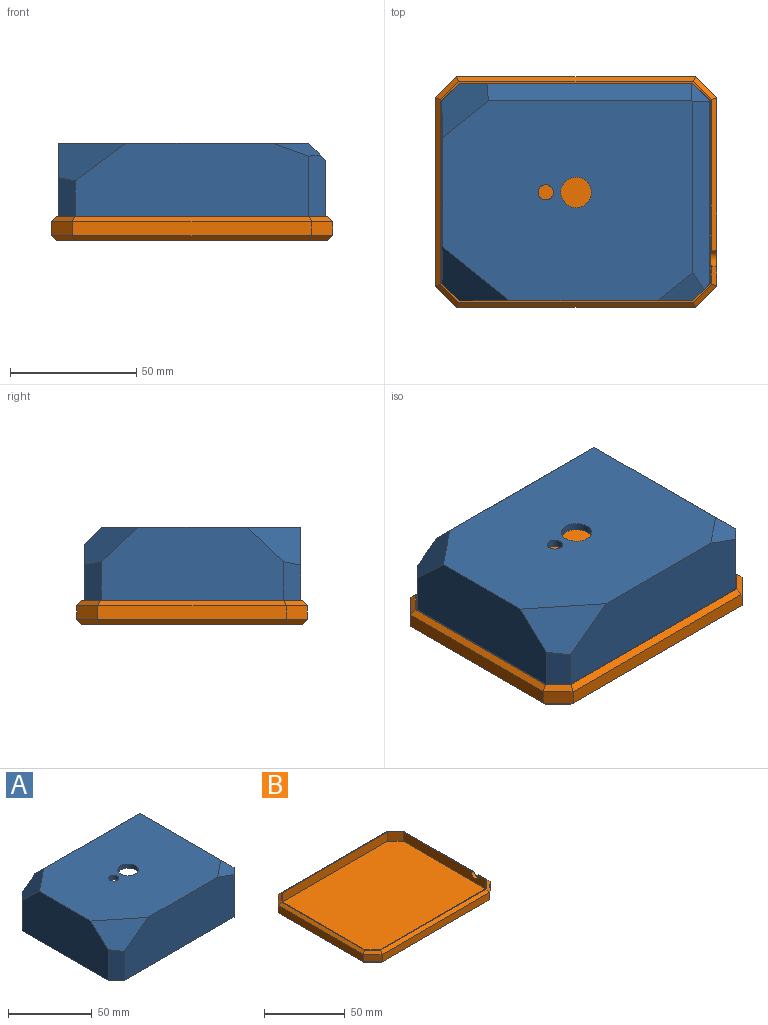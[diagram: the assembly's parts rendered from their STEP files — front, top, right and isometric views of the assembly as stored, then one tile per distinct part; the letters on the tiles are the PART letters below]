
ASSEMBLY  parts=2 mates=1
PART A: 34 faces, bbox 106x86x36 mm
  f0: plane 90x28mm, normal (0,-1,0), area 2479mm2, adj f6,f8,f9,f14,f20
  f1: plane 70x33mm, normal (1,0,0), area 2158.2mm2, adj f4,f5,f6,f13,f14,f20
  f2: plane 90x33mm, normal (0,1,0), area 2840.9mm2, adj f4,f5,f7,f12,f13,f20
  f3: plane 70x28mm, normal (-1,0,0), area 1931.7mm2, adj f9,f11,f12,f20,f33
  f4: plane 95x75mm, normal (0,0,-1), area 6640.7mm2, adj f1,f2,f5,f6,f7,f8,f11,f31
  f5: plane 22.21x17.77mm, normal (0.48,0.6,-0.64), area 287.6mm2, adj f1,f2,f4,f13
  f6: plane 17.77x15.96mm, normal (0.48,-0.6,-0.64), area 261.5mm2, adj f0,f1,f4,f8,f14
  f7: plane 13.59x8.17mm, normal (-0.31,0.39,-0.87), area 64.1mm2, adj f2,f4,f11,f12
  f8: plane 79.5x5mm, normal (0,-0.71,-0.71), area 560.5mm2, adj f0,f4,f6,f10
  f9: plane 28x5mm, normal (-0.71,-0.71,0), area 198mm2, adj f0,f3,f10,f20
  f10: plane 5x5mm, normal (-0.58,-0.58,-0.58), area 21.7mm2, adj f8,f9,f11
  f11: plane 71.62x5mm, normal (-0.71,0,-0.71), area 493.1mm2, adj f3,f4,f7,f10,f12
  f12: plane 29.62x5mm, normal (-0.71,0.71,0), area 206.9mm2, adj f2,f3,f7,f11,f20
  f13: plane 21.12x5mm, normal (0.71,0.71,0), area 146mm2, adj f1,f2,f5,f20
  f14: plane 21.12x5mm, normal (0.71,-0.71,0), area 146mm2, adj f0,f1,f6,f20
  f15: plane 92.49x29.24mm, normal (0,1,0), area 2660.3mm2, adj f20,f22,f24,f25,f26,f30
  f16: plane 72.49x36mm, normal (-1,0,0), area 2410.5mm2, adj f19,f20,f21,f22,f29,f30
  f17: plane 92.49x36mm, normal (0,-1,0), area 3146.1mm2, adj f19,f20,f21,f23,f28,f29
  f18: plane 72.49x29.24mm, normal (1,0,0), area 2091.3mm2, adj f20,f25,f26,f27,f28,f33
  f19: plane 99.24x79.24mm, normal (0,0,1), area 7224.2mm2, adj f16,f17,f21,f22,f23,f24,f26,f27
  f20: plane 106x86mm, normal (0,0,-1), area 1074.7mm2, adj f0,f1,f2,f3,f9,f12,f13,f14
  f21: plane 26.72x21.38mm, normal (-0.48,-0.6,0.64), area 408.9mm2, adj f16,f17,f19,f29
  f22: plane 21.38x18.28mm, normal (-0.48,0.6,0.64), area 361.2mm2, adj f15,f16,f19,f24,f30
  f23: plane 18.52x11.13mm, normal (0.31,-0.39,0.87), area 119mm2, adj f17,f19,f27,f28
  f24: plane 81.31x6.76mm, normal (0,0.71,0.71), area 774mm2, adj f15,f19,f22,f26
  f25: plane 28.95x6.76mm, normal (0.71,0.71,0), area 276.7mm2, adj f15,f18,f20,f26
  f26: plane 7.05x7.05mm, normal (0.58,0.58,0.58), area 46.4mm2, adj f15,f18,f19,f24,f25,f27
  f27: plane 74.35x6.76mm, normal (0.71,0,0.71), area 686mm2, adj f18,f19,f23,f26,f28
  f28: plane 31.4x6.76mm, normal (0.71,-0.71,0), area 295.4mm2, adj f17,f18,f20,f23,f27
  f29: plane 22.39x6.76mm, normal (-0.71,-0.71,0), area 208mm2, adj f16,f17,f20,f21
  f30: plane 22.39x6.76mm, normal (-0.71,0.71,0), area 208mm2, adj f15,f16,f20,f22
  f31: cylinder r=3mm len=6mm, axis (0,0,1), area 56.5mm2, adj f4,f19
  f32: cylinder r=6.05mm len=12.1mm, axis (0,0,1), area 114mm2, adj f4,f19
  f33: cylinder r=3mm len=6mm, axis (1,0,0), area 56.5mm2, adj f3,f18
PART B: 37 faces, bbox 111.4x91.4x9.5 mm
  f0: plane 74.72x5.5mm, normal (1,0,0), area 402mm2, adj f1,f5,f6,f20,f34,f36
  f1: plane 60.8x2.01mm, normal (0.71,0,0.71), area 170.4mm2, adj f0,f18,f32,f36
  f2: plane 74.72x5.5mm, normal (-1,0,0), area 411mm2, adj f3,f8,f27,f29
  f3: plane 8.34x8.34mm, normal (-0.71,-0.71,0), area 64.9mm2, adj f2,f4,f25,f31
  f4: plane 94.72x5.5mm, normal (0,-1,0), area 521mm2, adj f3,f5,f23,f33
  f5: plane 8.34x8.34mm, normal (0.71,-0.71,0), area 64.9mm2, adj f0,f4,f21,f35
  f6: plane 8.34x8.34mm, normal (0.71,0.71,0), area 64.9mm2, adj f0,f7,f22,f32
  f7: plane 94.72x5.5mm, normal (0,1,0), area 521mm2, adj f6,f8,f24,f30
  f8: plane 8.34x8.34mm, normal (-0.71,0.71,0), area 64.9mm2, adj f2,f7,f26,f28
  f9: plane 107.4x87.4mm, normal (0,0,-1), area 9284mm2, adj f20,f21,f22,f23,f24,f25,f26,f27
  f10: plane 7x6.87mm, normal (0.71,0.71,0), area 68.1mm2, adj f11,f17,f18,f19
  f11: plane 72.65x7mm, normal (1,0,0), area 508.6mm2, adj f10,f12,f18,f19
  f12: plane 7x6.87mm, normal (0.71,-0.71,0), area 68.1mm2, adj f11,f13,f18,f19
  f13: plane 92.65x7mm, normal (0,-1,0), area 648.6mm2, adj f12,f14,f18,f19
  f14: plane 7x6.87mm, normal (-0.71,-0.71,0), area 68.1mm2, adj f13,f15,f18,f19
  f15: plane 72.65x7mm, normal (-1,0,0), area 487.4mm2, adj f14,f16,f18,f19,f36
  f16: plane 7x6.87mm, normal (-0.71,0.71,0), area 68.1mm2, adj f15,f17,f18,f19
  f17: plane 92.65x7mm, normal (0,1,0), area 648.6mm2, adj f10,f16,f18,f19
  f18: plane 107.4x87.4mm, normal (0,0,1), area 182.6mm2, adj f1,f10,f11,f12,f13,f14,f15,f16
  f19: plane 106.4x86.4mm, normal (0,0,1), area 9098.4mm2, adj f10,f11,f12,f13,f14,f15,f16,f17
  f20: plane 74.72x2mm, normal (0.71,0,-0.71), area 209mm2, adj f0,f9,f21,f22
  f21: plane 9.17x9.17mm, normal (0.5,-0.5,-0.71), area 31mm2, adj f5,f9,f20,f23
  f22: plane 9.17x9.17mm, normal (0.5,0.5,-0.71), area 31mm2, adj f6,f9,f20,f24
  f23: plane 94.72x2mm, normal (0,-0.71,-0.71), area 265.6mm2, adj f4,f9,f21,f25
  f24: plane 94.72x2mm, normal (0,0.71,-0.71), area 265.6mm2, adj f7,f9,f22,f26
  f25: plane 9.17x9.17mm, normal (-0.5,-0.5,-0.71), area 31mm2, adj f3,f9,f23,f27
  f26: plane 9.17x9.17mm, normal (-0.5,0.5,-0.71), area 31mm2, adj f8,f9,f24,f27
  f27: plane 74.72x2mm, normal (-0.71,0,-0.71), area 209mm2, adj f2,f9,f25,f26
  f28: plane 9.17x9.17mm, normal (-0.5,0.5,0.71), area 31mm2, adj f8,f18,f29,f30
  f29: plane 74.72x2mm, normal (-0.71,0,0.71), area 209mm2, adj f2,f18,f28,f31
  f30: plane 94.72x2mm, normal (0,0.71,0.71), area 265.6mm2, adj f7,f18,f28,f32
  f31: plane 9.17x9.17mm, normal (-0.5,-0.5,0.71), area 31mm2, adj f3,f18,f29,f33
  f32: plane 9.17x9.17mm, normal (0.5,0.5,0.71), area 31mm2, adj f1,f6,f18,f30
  f33: plane 94.72x2mm, normal (0,-0.71,0.71), area 265.6mm2, adj f4,f18,f31,f35
  f34: plane 8.08x2.01mm, normal (0.71,0,0.71), area 21.3mm2, adj f0,f18,f35,f36
  f35: plane 9.17x9.17mm, normal (0.5,-0.5,0.71), area 31mm2, adj f5,f18,f33,f34
  f36: cylinder r=3.1mm len=6.2mm, axis (1,0,0), area 25.4mm2, adj f0,f1,f15,f18,f34
PLACE A t=(-132.45,-163.59,-42.72)mm
PLACE B t=(-132.45,-163.39,-48.22)mm
MATE fastened A.f17 <-> B.f17  axis (0,-1,0) through (-132.45,-206.59,-45.72)mm
